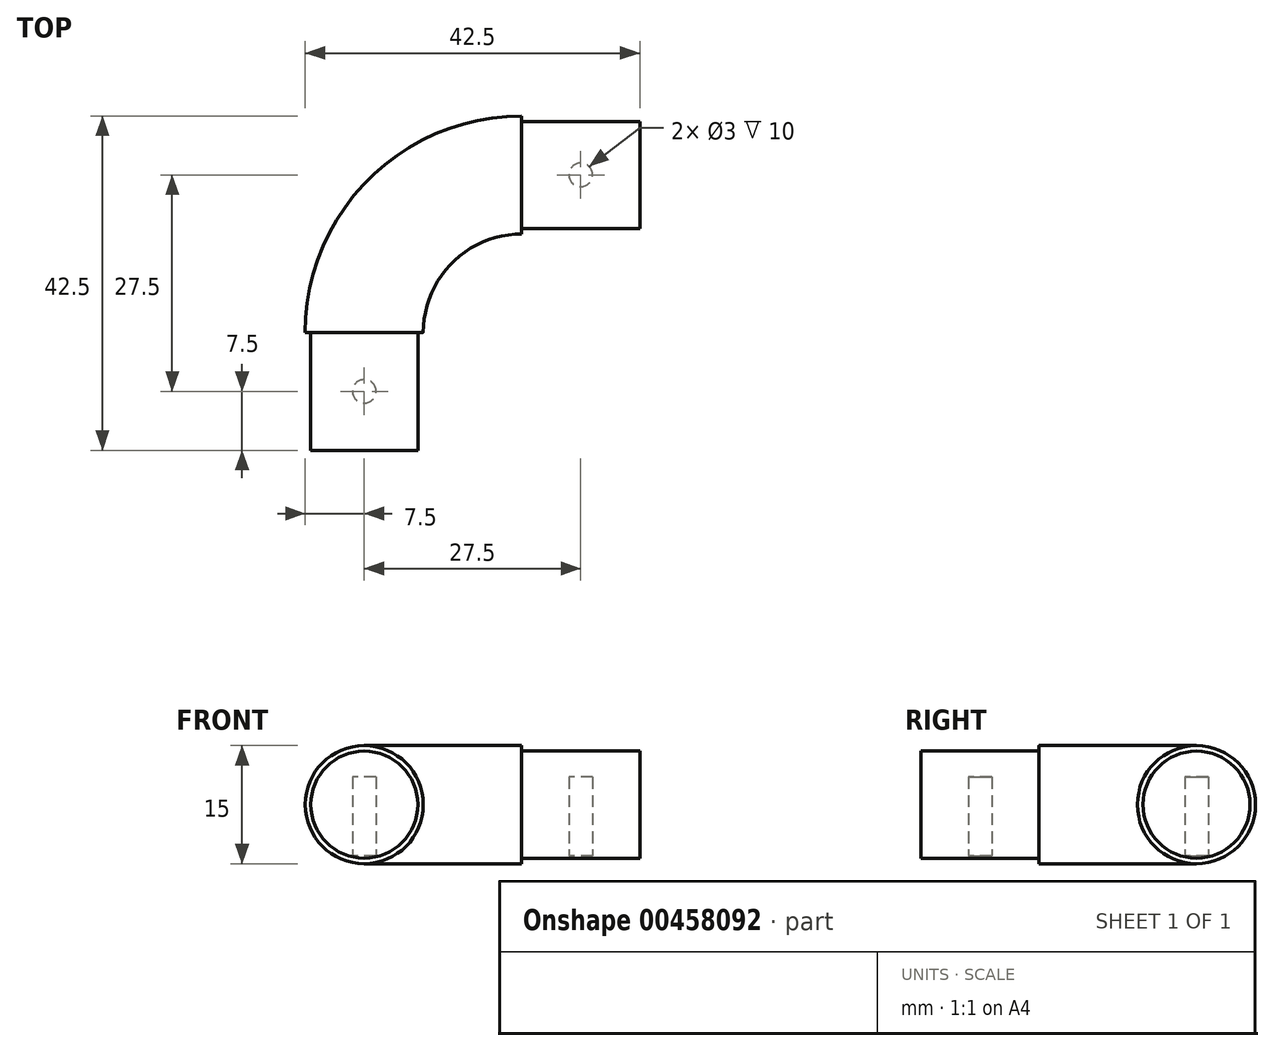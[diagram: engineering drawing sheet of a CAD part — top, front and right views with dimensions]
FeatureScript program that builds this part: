
annotation { "Feature Type Name" : "Feature", "Feature Type Description" : "" }
export const myFeature = defineFeature(function(context is Context, id is Id, definition is map)
    precondition{}
    {
        {
            var Q0;
            Q0=qCreatedBy(makeId("Top.planeOp"),FACE);
            var sketch = newSketch(context, id + "F0", { "sketchPlane" : qUnion([Q0])});
            skArc(sketch, "E0", {"start": v(20, 0) * mm, "mid": v(5.86, -5.86) * mm, "end": v(0, -20) * mm});
            skLineSegment(sketch, "E1", {"start": v(0, -20) * mm, "end": v(0, -35) * mm});
            skLineSegment(sketch, "E2", {"start": v(20, 0) * mm, "end": v(35, 0) * mm});
            skSolve(sketch);
        }
        {
            var Q0;
            Q0=qCreatedBy(makeId("Front.planeOp"),FACE);
            cPlane(context, id + "F1", {"entities" : qUnion([Q0]), "cplaneType" : CPlaneType.OFFSET, "offset" : 35 * mm, "width" : 150 * mm, "height" : 150 * mm});
        }
        {
            var Q0;
            Q0=qCreatedBy(makeId("Front.planeOp"),FACE);
            cPlane(context, id + "F2", {"entities" : qUnion([Q0]), "cplaneType" : CPlaneType.OFFSET, "offset" : 20 * mm, "width" : 150 * mm, "height" : 150 * mm});
        }
        {
            var Q0;
            Q0=qCreatedBy(id+"F2.planeOp",FACE);
            var sketch = newSketch(context, id + "F3", { "sketchPlane" : qUnion([Q0])});
            skCircle(sketch, "E3", {"center": v(0, 0) * mm, "radius": 7.5 * mm});
            skSolve(sketch);
        }
        {
            var Q0;
            Q0=qCreatedBy(id+"F1.planeOp",FACE);
            var sketch = newSketch(context, id + "F4", { "sketchPlane" : qUnion([Q0])});
            skCircle(sketch, "E4", {"center": v(0, 0) * mm, "radius": 6.8 * mm});
            skSolve(sketch);
        }
        {
            var Q0;
            Q0=qCreatedBy(makeId("Right.planeOp"),FACE);
            cPlane(context, id + "F5", {"entities" : qUnion([Q0]), "cplaneType" : CPlaneType.OFFSET, "offset" : 20 * mm, "width" : 150 * mm, "height" : 150 * mm});
        }
        {
            var Q0;
            Q0=qCreatedBy(makeId("Right.planeOp"),FACE);
            cPlane(context, id + "F6", {"entities" : qUnion([Q0]), "cplaneType" : CPlaneType.OFFSET, "offset" : 35 * mm, "width" : 150 * mm, "height" : 150 * mm});
        }
        {
            var Q0;
            Q0=qCreatedBy(id+"F6.planeOp",FACE);
            var sketch = newSketch(context, id + "F7", { "sketchPlane" : qUnion([Q0])});
            skCircle(sketch, "E5", {"center": v(0, 0) * mm, "radius": 6.8 * mm});
            skSolve(sketch);
        }
        {
            var Q0;
            Q0=makeQuery(id+"F3.imprint","IMPRINT",FACE,{"disambiguationData":[TD([[makeQuery(id+"F3.imprint","IMPRINT",EDGE,{"derivedFrom":sQuery(id+"F3.wireOp",EDGE,"E3")}),1.0]])]});
            var Q1;
            Q1=sQuery(id+"F0.wireOp",EDGE,"E0");
            sweep(context, id + "F8", {"profiles" : qUnion([Q0]), "path" : qUnion([Q1])});
        }
        {
            var Q0;
            Q0=makeQuery(id+"F4.imprint","IMPRINT",FACE,{"disambiguationData":[TD([[makeQuery(id+"F4.imprint","IMPRINT",EDGE,{"derivedFrom":sQuery(id+"F4.wireOp",EDGE,"E4")}),1.0]])]});
            var Q1;
            Q1=sQuery(id+"F0.wireOp",EDGE,"E1");
            sweep(context, id + "F9", {"profiles" : qUnion([Q0]), "path" : qUnion([Q1])});
        }
        {
            var Q0;
            Q0=makeQuery(id+"F7.imprint","IMPRINT",FACE,{"disambiguationData":[TD([[makeQuery(id+"F7.imprint","IMPRINT",EDGE,{"derivedFrom":sQuery(id+"F7.wireOp",EDGE,"E5")}),1.0]])]});
            var Q1;
            Q1=sQuery(id+"F0.wireOp",EDGE,"E2");
            sweep(context, id + "F10", {"operationType" : NewBodyOperationType.ADD, "profiles" : qUnion([Q0]), "path" : qUnion([Q1])});
        }
        {
            var Q0;
            Q0=qCreatedBy(makeId("Top.planeOp"),FACE);
            cPlane(context, id + "F11", {"entities" : qUnion([Q0]), "cplaneType" : CPlaneType.OFFSET, "offset" : 6.5 * mm, "oppositeDirection" : true, "width" : 150 * mm, "height" : 150 * mm});
        }
        {
            var Q0;
            Q0=qCreatedBy(id+"F11.planeOp",FACE);
            var sketch = newSketch(context, id + "F12", { "sketchPlane" : qUnion([Q0])});
            skCircle(sketch, "E6", {"center": v(0, -27.5) * mm, "radius": 1.5 * mm});
            skCircle(sketch, "E7", {"center": v(27.5, 0) * mm, "radius": 1.5 * mm});
            skSolve(sketch);
        }
        {
            var Q0;
            Q0 = qSketchRegion(id + "F12", true);
            extrude(context, id + "F13", {"entities" : qUnion([Q0]), "operationType" : NewBodyOperationType.REMOVE, "depth" : 10 * mm});
        }
    });
